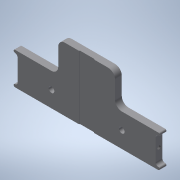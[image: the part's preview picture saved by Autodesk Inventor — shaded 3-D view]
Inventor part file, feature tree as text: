
AUTODESK INVENTOR PART (.ipt)
format: ipt  version: 2022 (Build 260153000, 153)  size: 190,464 bytes
history: native  units: mm
features: sketch x7, extrude x4, fillet x4, hole x3, plane x1
ambient origin geometry x8: Origin, YZ Plane, XZ Plane, XY Plane, X Axis, Y Axis, Z Axis, Center Point
bodies: Volumenkörper1 (feature_tree)
feature tree (19):
  extrude  "Extrusion1"  Depth=24.0mm
  extrude  "Extrusion2"  Depth=23.0mm
  extrude  "Extrusion3"  Depth=5.0mm TaperAngle=0.0deg
  fillet  "Rundung1"  Radius=2.0mm
  fillet  "Rundung2"  Radius=2.0mm
  extrude  "Extrusion4"  Depth=2.0mm
  hole  "Bohrung2"  [1 undecoded]
  hole  "Bohrung3"  [1 undecoded]
  hole  "Bohrung4"  [1 undecoded]
  plane  "Arbeitsebene1"
  fillet  "Rundung3"  Radius=3.0mm
  fillet  "Rundung4"  Radius=12.0mm
  sketch  "Skizze1"  dims[d0=108.0mm d1=24.0mm]
  sketch  "Skizze2"  dims[d2=33.0mm d3=23.0mm]
  sketch  "Skizze3"  dims[d4=42.0mm d5=5.0mm d6=0.0mm d7=2.0mm d8=2.0mm]
  sketch  "Skizze4"  dims[d9=3.0mm d10=0.0mm d11=2.0mm]
  sketch  "Skizze6"  dims[d12=2.0mm d13=3.0mm d14=0.0mm]
  sketch  "Skizze7"  dims[d15=1.0mm d16=5.0mm]
  sketch  "Skizze8"  dims[d17=11.0mm d18=1.0mm d19=3.0mm d20=0.0mm d31=12.0mm d32=26.0mm d33=26.0mm d34=4.2mm d35=4.2mm d36=8.4mm d37=2.0mm d38=90.0deg d39=8.0mm d40=20.594885mm d41=2.5mm d42=10.0mm d43=2.459mm d44=5.0mm d45=3.023mm d46=2.0mm d47=14.3117mm d48=6.0mm d49=20.594885mm d50=2.5mm d51=10.0mm d52=2.459mm d53=5.0mm d54=3.023mm d55=2.0mm d56=14.3117mm d57=6.0mm d58=20.594885mm d59=2.0mm d60=2.0mm]
note: 3 required parameter values undecoded (feature->parameter linkage not recoverable at this tier; creation-order binding heuristic only, values carry confidence <= 0.55)
